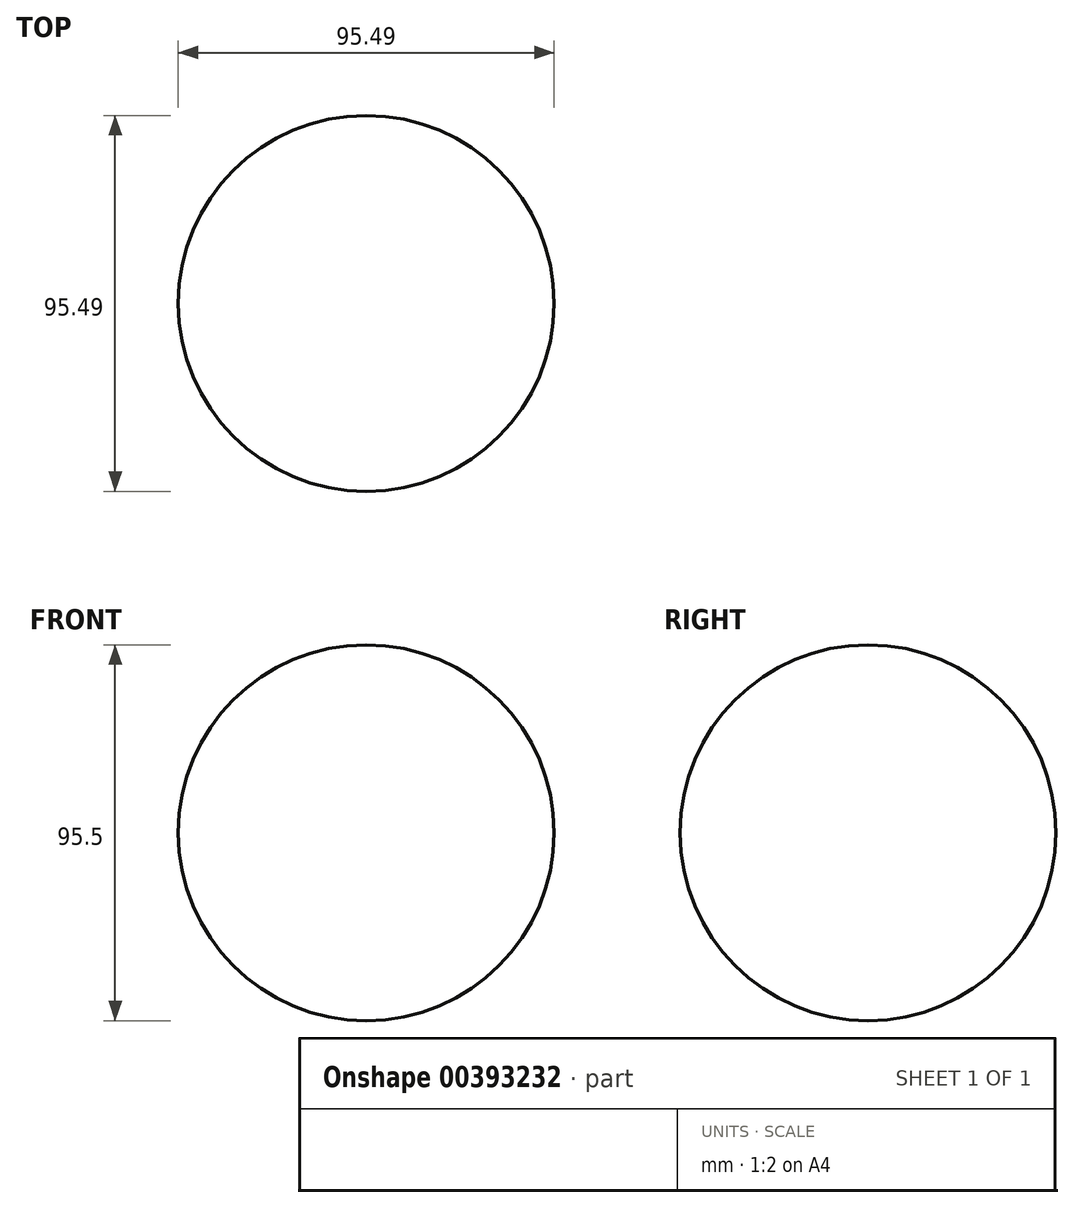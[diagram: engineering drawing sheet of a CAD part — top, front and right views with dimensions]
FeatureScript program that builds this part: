
annotation { "Feature Type Name" : "Feature", "Feature Type Description" : "" }
export const myFeature = defineFeature(function(context is Context, id is Id, definition is map)
    precondition{}
    {
        {
            var Q0;
            Q0=qCreatedBy(makeId("Top.planeOp"),FACE);
            var sketch = newSketch(context, id + "F0", { "sketchPlane" : qUnion([Q0])});
            skCircle(sketch, "E0", {"center": v(4.02, 75.17) * mm, "radius": 47.75 * mm});
            skLineSegment(sketch, "E1", {"start": v(4.02, 122.92) * mm, "end": v(4.02, 27.43) * mm});
            skSolve(sketch);
        }
        {
            var Q0;
            {var subQ0=sQuery(id+"F0.wireOp",EDGE,"E1");Q0=makeQuery(id+"F0.imprint","IMPRINT",FACE,{"disambiguationData":[TD([[makeQuery(id+"F0.imprint","IMPRINT",EDGE,{"derivedFrom":subQ0}),-1.0]])]});}
            var Q1;
            Q1=sQuery(id+"F0.wireOp",EDGE,"E1");
            revolve(context, id + "F1", {"entities" : qUnion([Q0]), "axis" : qUnion([Q1]), "revolveType" : RevolveType.FULL});
        }
    });
